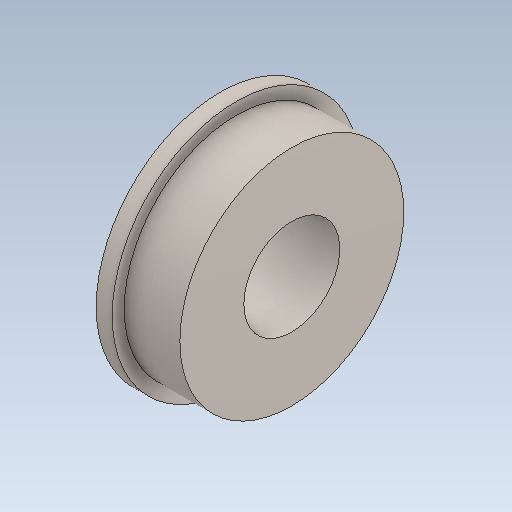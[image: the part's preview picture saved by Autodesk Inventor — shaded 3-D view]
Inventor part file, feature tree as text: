
AUTODESK INVENTOR PART (.ipt)
format: ipt  version: 2020 (Build 240168000, 168)  size: 138,240 bytes
history: native  units: in
note: dims shown in document units (in); Inventor stores cm internally (conversion verified against a paired STEP export)
features: revolve x1
ambient origin geometry x8: Origin, YZ Plane, XZ Plane, XY Plane, X Axis, Y Axis, Z Axis, Center Point
bodies: Solid1 (feature_tree)
feature tree (1):
  revolve  "Revolve1"  [1 undecoded]
note: 1 required parameter value undecoded (feature->parameter linkage not recoverable at this tier; creation-order binding heuristic only, values carry confidence <= 0.55)
